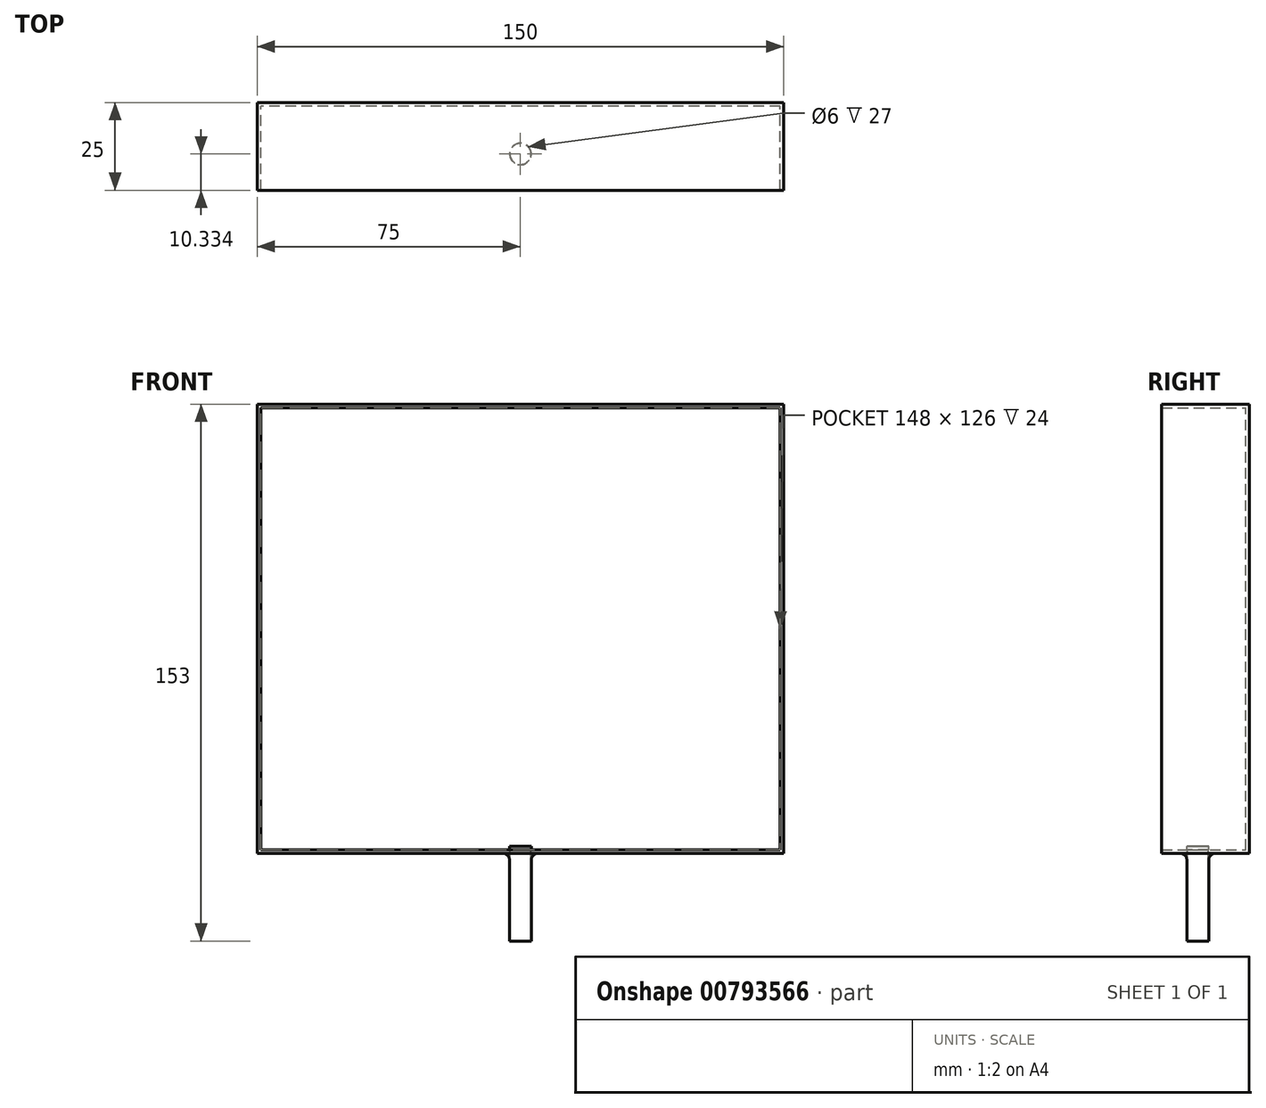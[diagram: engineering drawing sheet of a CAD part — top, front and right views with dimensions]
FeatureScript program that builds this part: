
annotation { "Feature Type Name" : "Feature", "Feature Type Description" : "" }
export const myFeature = defineFeature(function(context is Context, id is Id, definition is map)
    precondition{}
    {
        {
            var Q0;
            Q0=qCreatedBy(makeId("Front.planeOp"),FACE);
            var sketch = newSketch(context, id + "F0", { "sketchPlane" : qUnion([Q0])});
            skLineSegment(sketch, "E0.bottom", {"start": v(75, -64) * mm, "end": v(-75, -64) * mm});
            skLineSegment(sketch, "E0.top", {"start": v(75, 64) * mm, "end": v(-75, 64) * mm});
            skLineSegment(sketch, "E0.left", {"start": v(75, -64) * mm, "end": v(75, 64) * mm});
            skLineSegment(sketch, "E0.right", {"start": v(-75, -64) * mm, "end": v(-75, 64) * mm});
            skPoint(sketch, "E0.middle", {"position": v(0, 0) * mm});
            skSolve(sketch);
        }
        {
            var Q0;
            Q0=makeQuery(id+"F0.imprint","IMPRINT",FACE,{"disambiguationData":[TD([[makeQuery(id+"F0.imprint","IMPRINT",EDGE,{"derivedFrom":sQuery(id+"F0.wireOp",EDGE,"E0.bottom")}),-1.0]])]});
            extrude(context, id + "F1", {"entities" : qUnion([Q0]), "depth" : 25 * mm, "offsetDistance" : 25 * mm});
        }
        {
            var Q0;
            Q0=makeQuery(id+"F1.opExtrude","CAP_FACE",FACE,{"disambiguationData":[OSD([sQuery(id+"F0.wireOp",EDGE,"E0.bottom"),sQuery(id+"F0.wireOp",EDGE,"E0.top"),sQuery(id+"F0.wireOp",EDGE,"E0.left"),sQuery(id+"F0.wireOp",EDGE,"E0.right")])],"isStart":false});
            shell(context, id + "F2", {"entities" : qUnion([Q0]), "thickness" : 1 * mm});
        }
        {
            var Q0;
            Q0=makeQuery(id+"F1.opExtrude","SWEPT_FACE",FACE,{"disambiguationData":[OSD([sQuery(id+"F0.wireOp",EDGE,"E0.bottom")])]});
            var sketch = newSketch(context, id + "F3", { "sketchPlane" : qUnion([Q0])});
            skPoint(sketch, "E1", {"position": v(0, 14.67) * mm});
            skCircle(sketch, "E2", {"center": v(0, 14.67) * mm, "radius": 3.1 * mm});
            skSolve(sketch);
        }
        {
            var Q0;
            Q0=makeQuery(id+"F3.imprint","IMPRINT",FACE,{"disambiguationData":[TD([[makeQuery(id+"F3.imprint","IMPRINT",EDGE,{"derivedFrom":sQuery(id+"F3.wireOp",EDGE,"E2")}),1.0]])]});
            extrude(context, id + "F4", {"entities" : qUnion([Q0]), "operationType" : NewBodyOperationType.ADD, "depth" : 25 * mm, "offsetDistance" : 25 * mm, "hasSecondDirection" : true, "secondDirectionOppositeDirection" : true, "secondDirectionDepth" : 2 * mm});
        }
        {
            var Q0;
            Q0=sQuery(id+"F3.wireOp",VERTEX,"E1");
            var Q1;
            Q1=makeQuery(id+"F1.opExtrude","SWEPT_BODY",BODY,{"disambiguationData":[OSD([sQuery(id+"F0.wireOp",EDGE,"E0.bottom"),sQuery(id+"F0.wireOp",EDGE,"E0.top"),sQuery(id+"F0.wireOp",EDGE,"E0.left"),sQuery(id+"F0.wireOp",EDGE,"E0.right")])]});
            hole(context, id + "F5", {"style" : HoleStyle.SIMPLE, "endStyle" : HoleEndStyle.BLIND, "oppositeDirection" : true, "holeDiameter" : 6 * mm, "majorDiameter" : 5 * mm, "holeDepth" : 25 * mm, "isTappedThrough" : true, "tappedDepth" : 12 * mm, "tapClearance" : 3, "startFromSketch" : true, "locations" : qUnion([Q0]), "scope" : qUnion([Q1])});
        }
        {
            var Q0;
            Q0=sQuery(id+"F3.wireOp",VERTEX,"E1");
            var Q1;
            Q1=makeQuery(id+"F1.opExtrude","SWEPT_BODY",BODY,{"disambiguationData":[OSD([sQuery(id+"F0.wireOp",EDGE,"E0.bottom"),sQuery(id+"F0.wireOp",EDGE,"E0.top"),sQuery(id+"F0.wireOp",EDGE,"E0.left"),sQuery(id+"F0.wireOp",EDGE,"E0.right")])]});
            hole(context, id + "F6", {"style" : HoleStyle.SIMPLE, "endStyle" : HoleEndStyle.BLIND, "holeDiameter" : 6 * mm, "majorDiameter" : 5 * mm, "holeDepth" : 25 * mm, "isTappedThrough" : true, "tappedDepth" : 12 * mm, "tapClearance" : 3, "startFromSketch" : true, "locations" : qUnion([Q0]), "scope" : qUnion([Q1])});
        }
        {
            var Q0;
            Q0=makeQuery(id+"F4.boolean.opBoolean","INTERSECT",EDGE,{"derivedFrom":[makeQuery(id+"F1.opExtrude","SWEPT_FACE",FACE,{"disambiguationData":[OSD([sQuery(id+"F0.wireOp",EDGE,"E0.bottom")])]}),makeQuery(id+"F4.opExtrude","SWEPT_FACE",FACE,{"disambiguationData":[OSD([sQuery(id+"F3.wireOp",EDGE,"E2")])]})]});
            fillet(context, id + "F7", {"entities" : qUnion([Q0]), "radius" : 2 * mm, "tangentPropagation" : true, "allowEdgeOverflow" : false});
        }
    });
